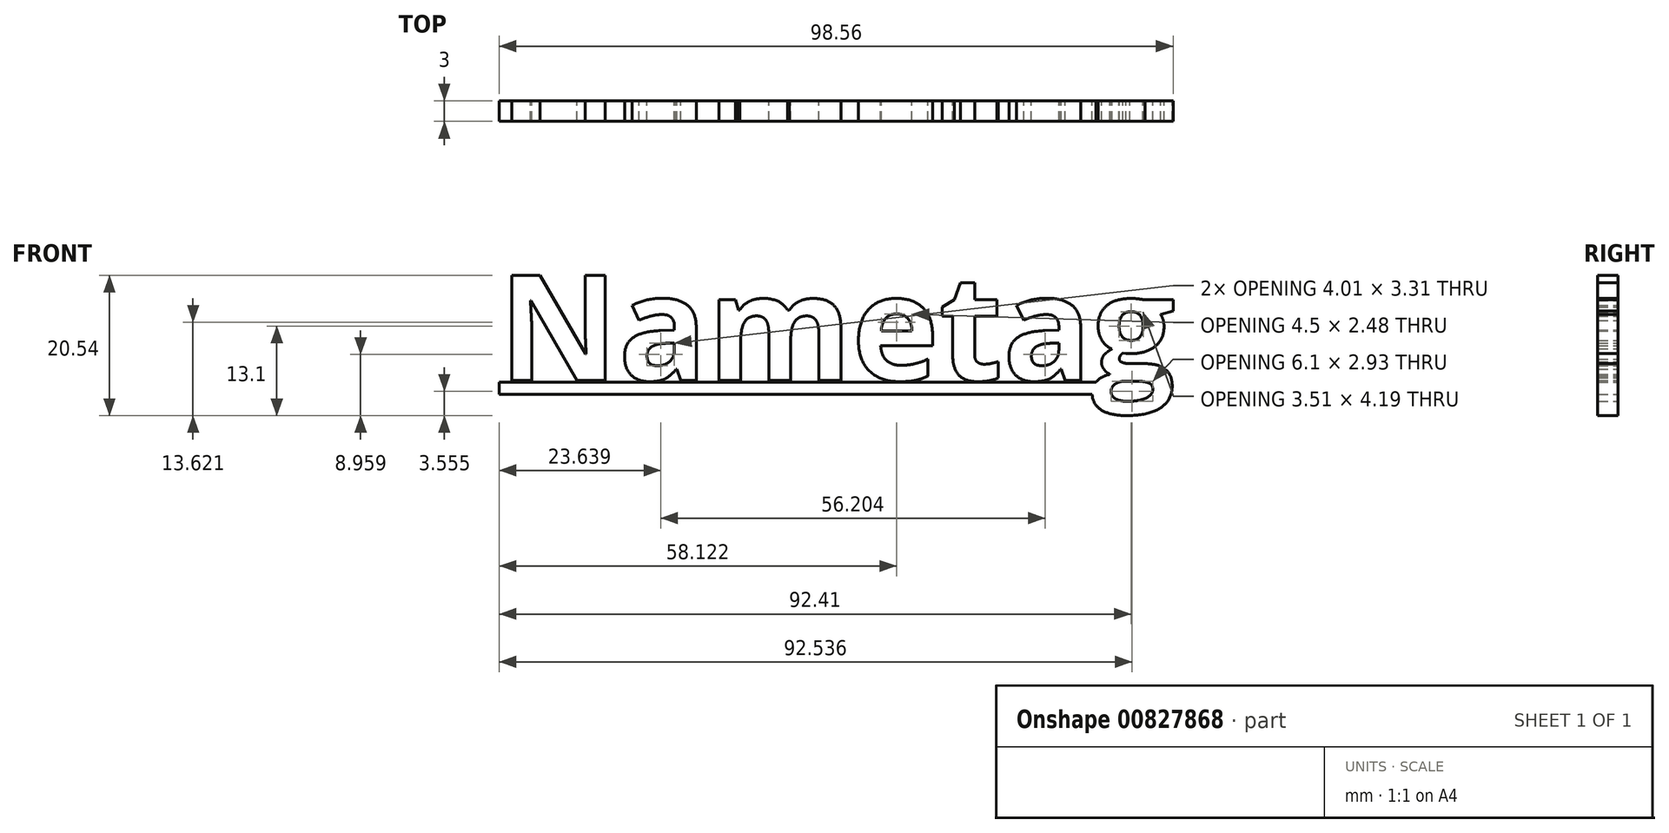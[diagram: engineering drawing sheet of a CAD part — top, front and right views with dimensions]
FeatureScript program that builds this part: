
annotation { "Feature Type Name" : "Feature", "Feature Type Description" : "" }
export const myFeature = defineFeature(function(context is Context, id is Id, definition is map)
    precondition{}
    {
        {
            var Q0;
            Q0=qCreatedBy(makeId("Front.planeOp"),FACE);
            var sketch = newSketch(context, id + "F0", { "sketchPlane" : qUnion([Q0])});
            skText(sketch, "E0", { "text": "Nametag", "fontName": "OpenSans-Bold.ttf"});
            const initialGuessF0  = {"E0": [-0.04936, 0.00028, 1, 0, 0.0155]};
            skSetInitialGuess(sketch, initialGuessF0);
            skSolve(sketch);
        }
        {
            var Q0;
            Q0 = qSketchRegion(id + "F0", true);
            extrude(context, id + "F1", {"entities" : qUnion([Q0]), "depth" : 3 * mm, "offsetDistance" : 25 * mm});
        }
        {
            var Q0;
            Q0=makeQuery(id+"F1.opExtrude","CAP_FACE",FACE,{"disambiguationData":[OSD([sQuery(id+"F0.wireOp",EDGE,"E0.sketch_text.stroke-39"),sQuery(id+"F0.wireOp",EDGE,"E0.sketch_text.stroke-40"),sQuery(id+"F0.wireOp",EDGE,"E0.sketch_text.stroke-41"),sQuery(id+"F0.wireOp",EDGE,"E0.sketch_text.stroke-42"),sQuery(id+"F0.wireOp",EDGE,"E0.sketch_text.stroke-43"),sQuery(id+"F0.wireOp",EDGE,"E0.sketch_text.stroke-44"),sQuery(id+"F0.wireOp",EDGE,"E0.sketch_text.stroke-45"),sQuery(id+"F0.wireOp",EDGE,"E0.sketch_text.stroke-46"),sQuery(id+"F0.wireOp",EDGE,"E0.sketch_text.stroke-47"),sQuery(id+"F0.wireOp",EDGE,"E0.sketch_text.stroke-48"),sQuery(id+"F0.wireOp",EDGE,"E0.sketch_text.stroke-49"),sQuery(id+"F0.wireOp",EDGE,"E0.sketch_text.stroke-50"),sQuery(id+"F0.wireOp",EDGE,"E0.sketch_text.stroke-51"),sQuery(id+"F0.wireOp",EDGE,"E0.sketch_text.stroke-52"),sQuery(id+"F0.wireOp",EDGE,"E0.sketch_text.stroke-53"),sQuery(id+"F0.wireOp",EDGE,"E0.sketch_text.stroke-54"),sQuery(id+"F0.wireOp",EDGE,"E0.sketch_text.stroke-55"),sQuery(id+"F0.wireOp",EDGE,"E0.sketch_text.stroke-56"),sQuery(id+"F0.wireOp",EDGE,"E0.sketch_text.stroke-57"),sQuery(id+"F0.wireOp",EDGE,"E0.sketch_text.stroke-58"),sQuery(id+"F0.wireOp",EDGE,"E0.sketch_text.stroke-59"),sQuery(id+"F0.wireOp",EDGE,"E0.sketch_text.stroke-60"),sQuery(id+"F0.wireOp",EDGE,"E0.sketch_text.stroke-61"),sQuery(id+"F0.wireOp",EDGE,"E0.sketch_text.stroke-62"),sQuery(id+"F0.wireOp",EDGE,"E0.sketch_text.stroke-63"),sQuery(id+"F0.wireOp",EDGE,"E0.sketch_text.stroke-64"),sQuery(id+"F0.wireOp",EDGE,"E0.sketch_text.stroke-65"),sQuery(id+"F0.wireOp",EDGE,"E0.sketch_text.stroke-66")])],"isStart":false});
            var sketch = newSketch(context, id + "F2", { "sketchPlane" : qUnion([Q0])});
            skLineSegment(sketch, "E1.bottom", {"start": v(-49.3, 0) * mm, "end": v(38.43, 0) * mm});
            skLineSegment(sketch, "E1.top", {"start": v(-49.3, -1.78) * mm, "end": v(38.43, -1.78) * mm});
            skLineSegment(sketch, "E1.left", {"start": v(-49.3, 0) * mm, "end": v(-49.3, -1.78) * mm});
            skLineSegment(sketch, "E1.right", {"start": v(38.43, 0) * mm, "end": v(38.43, -1.78) * mm});
            skSolve(sketch);
        }
        {
            var Q0;
            Q0 = qSketchRegion(id + "F2", true);
            extrude(context, id + "F3", {"entities" : qUnion([Q0]), "operationType" : NewBodyOperationType.ADD, "oppositeDirection" : true, "depth" : 3 * mm, "offsetDistance" : 25 * mm});
        }
    });
